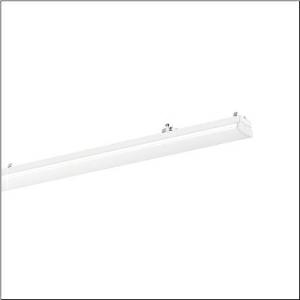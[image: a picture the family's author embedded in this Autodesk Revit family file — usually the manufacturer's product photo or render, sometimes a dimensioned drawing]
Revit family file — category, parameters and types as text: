
# Revit family: licross_r__21_recessed_opal_mo_52tl1d7n44xg_713e
name_source: partatom
category: Lighting Fixtures
units: mm (PartAtom-declared; Revit-internal decimal feet)

## family parameters
Cut with Voids When Loaded = No
Host = Face
Light Source = No
Part Type = Normal
Room Calculation Point = No
Round Connector Dimension = Use Diameter
Shared = No

## types (1)
- Licross® 21 recessed opal MO (1 x LED, 4400 lm, 24.7 W, 4000K)
    Apparent Load = 25 VA
    CIE Flux Codes = 44 73 91 87 100
    Color Rendering = 80
    Color Temperature = 4000K
    Default Elevation = 1800 mm
    Description = Licross® 21 recessed opal MO, luminaire insert, of sheet steel, galvanised, coil coated, white, length: 1.500mm, width: 66mm, height: 67mm, LED rated luminous flux: 4.400lm, light colour: 840, control gear: ON/OFF, with plug, 3-pole, with phase selection, mains connection: 220..240V, AC, 50/60Hz, rated input power: 25W, internal wiring halogen-free, primary optical cover: cover, of PMMA, light emission: direct with ceiling illumination distribution, primary light characteristic: symmetric, protection rating (complete): IP40, insulation class (complete): insulation class I (protective earthing), certification: CE, ENEC, VDE, UKCA, protection symbol: D if used in an environment without relevant dust loads with corresponding accessories, impact resistance: IK06, permissible ambient temperature for indoor applications: -35..+50°C, corresponds to IFS (International Featured Standards) requirements for safety and quality in the food industry, reducing of maximum allowable ambient temperature of 5°C with ceiling mounting, LABS conformity tested according to VDMA 24364:2018-05, packaging unit: 1 piece
    Height = 83 mm
    Lamp = 1 x LED
    Lamp Light Flux = 4400 lm
    Lamp Power = 24.7 W
    Lamp count = 1
    Length = 1500 mm
    Luminous efficacy = 178 lm/W
    Manufacturer = Siteco
    ModVariant = No
    Model = 52TL1D7N44XG
    Mounting Place = Ceiling
    Mounting Type = Pendant
    Number of Poles = 1
    OnlyDefault = Yes
    Power Factor = 1
    Product Name = Licross® 21 recessed opal MO
    Product group = luminaire insert | ceiling pendant
    ProductGroupID = 902
    Protection Class = Protection class I
    Protection Degree = IP 40
    RLX_Detail_Level = 1
    RLX_Emergency_Light_Flux = 0 lm
    RLX_Emergency_Type = 0
    RLX_Emergency_Type_DB = No
    RlxData = <blob elided: 23197 chars, md5=f08c5d8a>
    Socket = socket
    Standby Power = 0 W
    System Light Flux = 4400 lm
    System Power = 25 W
    Type Comments = Product without accessories
    Type Image = l_1313666.jpg
    URL = http://relux.com
    VarID = ---
    Voltage = 0 V
    Weight = 0.00 kg
    Width = 76 mm

## geometry (parser evidence)
native form markers: Blend x4, Sweep x12
no freeform markers — native parametric forms only
